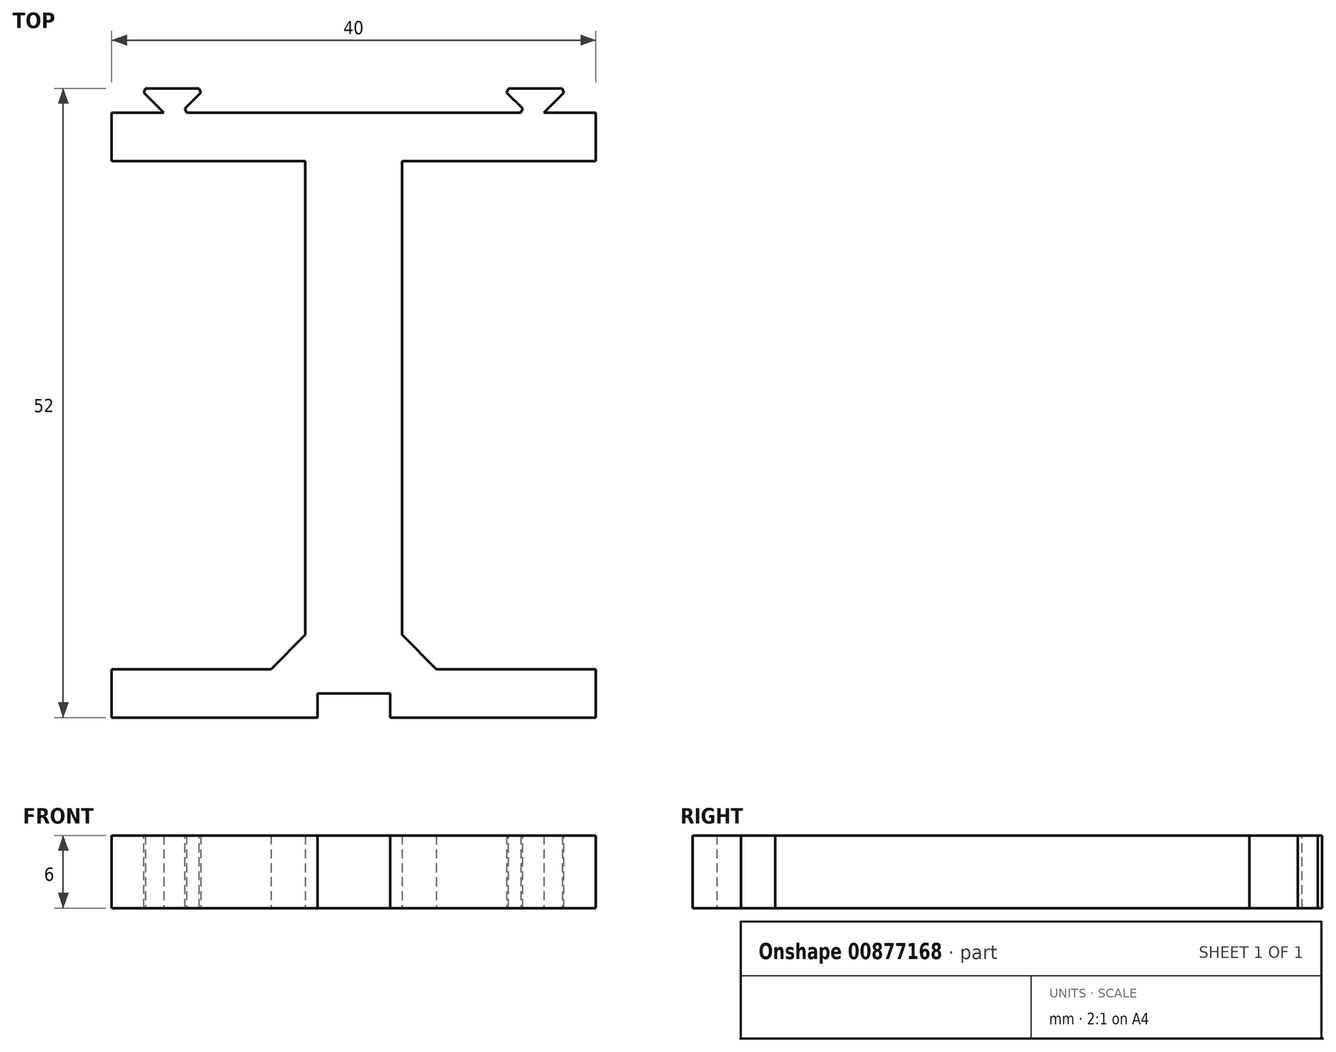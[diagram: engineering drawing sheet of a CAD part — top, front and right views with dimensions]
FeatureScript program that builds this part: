
annotation { "Feature Type Name" : "Feature", "Feature Type Description" : "" }
export const myFeature = defineFeature(function(context is Context, id is Id, definition is map)
    precondition{}
    {
        {
            var Q0;
            Q0=qCreatedBy(makeId("Top.planeOp"),FACE);
            var sketch = newSketch(context, id + "F0", { "sketchPlane" : qUnion([Q0])});
            skLineSegment(sketch, "E0.bottom", {"start": v(0, 0) * mm, "end": v(20, 0) * mm});
            skLineSegment(sketch, "E0.top", {"start": v(0, -50) * mm, "end": v(20, -50) * mm});
            skLineSegment(sketch, "E0.left", {"start": v(0, 0) * mm, "end": v(0, -50) * mm});
            skLineSegment(sketch, "E0.right", {"start": v(20, 0) * mm, "end": v(20, -50) * mm, "construction": true});
            skLineSegment(sketch, "E1.0", {"start": v(4, -46) * mm, "end": v(16, -46) * mm});
            skLineSegment(sketch, "E1.1", {"start": v(4, -4) * mm, "end": v(4, -46) * mm});
            skLineSegment(sketch, "E1.2", {"start": v(4, -4) * mm, "end": v(16, -4) * mm});
            skLineSegment(sketch, "E1.3", {"start": v(16, -4) * mm, "end": v(16, -46) * mm, "construction": true});
            skLineSegment(sketch, "E2", {"start": v(16, -4) * mm, "end": v(20, -4) * mm});
            skLineSegment(sketch, "E3", {"start": v(16, -46) * mm, "end": v(20, -46) * mm});
            skLineSegment(sketch, "E4", {"start": v(20, 0) * mm, "end": v(20, -4) * mm});
            skLineSegment(sketch, "E5", {"start": v(20, -46) * mm, "end": v(20, -50) * mm});
            skLineSegment(sketch, "E6.bottom", {"start": v(0, -50) * mm, "end": v(3, -50) * mm});
            skLineSegment(sketch, "E6.top", {"start": v(0, -48) * mm, "end": v(3, -48) * mm});
            skLineSegment(sketch, "E6.left", {"start": v(0, -50) * mm, "end": v(0, -48) * mm});
            skLineSegment(sketch, "E6.right", {"start": v(3, -50) * mm, "end": v(3, -48) * mm});
            skLineSegment(sketch, "E7", {"start": v(4, -43.17) * mm, "end": v(6.83, -46) * mm});
            skSolve(sketch);
        }
        {
            var Q0;
            {var subQ3=sQuery(id+"F0.wireOp",EDGE,"E7");Q0=makeQuery(id+"F0.imprint","IMPRINT",FACE,{"disambiguationData":[TD([[makeQuery(id+"F0.imprint","IMPRINT",EDGE,{"derivedFrom":subQ3}),-1.0]])]});}
            var Q1;
            Q1=makeQuery(id+"F0.imprint","IMPRINT",FACE,{"disambiguationData":[TD([[makeQuery(id+"F0.imprint","IMPRINT",EDGE,{"derivedFrom":sQuery(id+"F0.wireOp",EDGE,"E0.bottom")}),-1.0]])]});
            extrude(context, id + "F1", {"entities" : qUnion([Q0, Q1]), "depth" : 6 * mm, "offsetDistance" : 25 * mm});
        }
        {
            var Q0;
            Q0=qCreatedBy(makeId("Top.planeOp"),FACE);
            var sketch = newSketch(context, id + "F2", { "sketchPlane" : qUnion([Q0])});
            skLineSegment(sketch, "E8", {"start": v(20, 0) * mm, "end": v(15.7, 0) * mm, "construction": true});
            skLineSegment(sketch, "E9", {"start": v(15.7, 0) * mm, "end": v(17.7, 2) * mm});
            skLineSegment(sketch, "E10", {"start": v(17.7, 2) * mm, "end": v(12.3, 2) * mm});
            skLineSegment(sketch, "E11", {"start": v(12.3, 2) * mm, "end": v(14.3, 0) * mm});
            skLineSegment(sketch, "E12", {"start": v(14.3, 0) * mm, "end": v(15.7, 0) * mm});
            skLineSegment(sketch, "E13", {"start": v(15, 0) * mm, "end": v(15, 2) * mm, "construction": true});
            skSolve(sketch);
        }
        {
            var Q0;
            Q0 = qSketchRegion(id + "F2", true);
            var Q1;
            Q1=makeQuery(id+"F1.opExtrude","CAP_FACE",FACE,{"disambiguationData":[OSD([sQuery(id+"F0.wireOp",EDGE,"E0.bottom"),sQuery(id+"F0.wireOp",EDGE,"E0.top"),sQuery(id+"F0.wireOp",EDGE,"E0.left"),sQuery(id+"F0.wireOp",EDGE,"E1.0"),sQuery(id+"F0.wireOp",EDGE,"E1.1"),sQuery(id+"F0.wireOp",EDGE,"E1.2"),sQuery(id+"F0.wireOp",EDGE,"E2"),sQuery(id+"F0.wireOp",EDGE,"E3"),sQuery(id+"F0.wireOp",EDGE,"E4"),sQuery(id+"F0.wireOp",EDGE,"E5"),sQuery(id+"F0.wireOp",EDGE,"E6.top"),sQuery(id+"F0.wireOp",EDGE,"E6.right"),sQuery(id+"F0.wireOp",EDGE,"E7")])],"isStart":false});
            extrude(context, id + "F3", {"entities" : qUnion([Q0]), "operationType" : NewBodyOperationType.ADD, "endBound" : BoundingType.UP_TO_SURFACE, "depth" : 25 * mm, "endBoundEntityFace" : qUnion([Q1]), "offsetDistance" : 25 * mm});
        }
        {
            var Q0;
            Q0=makeQuery(id+"F3.opExtrude","SWEPT_EDGE",EDGE,{"disambiguationData":[OSD([sQuery(id+"F2.wireOp",EDGE,"E9"),sQuery(id+"F2.wireOp",EDGE,"E10")])]});
            var Q1;
            Q1=makeQuery(id+"F3.opExtrude","SWEPT_EDGE",EDGE,{"disambiguationData":[OSD([sQuery(id+"F2.wireOp",EDGE,"E10"),sQuery(id+"F2.wireOp",EDGE,"E11")])]});
            var Q2;
            Q2=makeQuery(id+"F3.opExtrude","SWEPT_EDGE",EDGE,{"disambiguationData":[OSD([sQuery(id+"F2.wireOp",EDGE,"E9"),sQuery(id+"F2.wireOp",EDGE,"E12")])]});
            var Q3;
            Q3=makeQuery(id+"F3.opExtrude","SWEPT_EDGE",EDGE,{"disambiguationData":[OSD([sQuery(id+"F2.wireOp",EDGE,"E11"),sQuery(id+"F2.wireOp",EDGE,"E12")])]});
            chamfer(context, id + "F4", {"entities" : qUnion([Q0, Q1, Q2, Q3]), "width" : 0.2 * mm, "tangentPropagation" : true});
        }
        {
            var Q0;
            Q0=makeQuery(id+"F1.opExtrude","SWEPT_BODY",BODY,{"disambiguationData":[OSD([sQuery(id+"F0.wireOp",EDGE,"E0.bottom"),sQuery(id+"F0.wireOp",EDGE,"E0.top"),sQuery(id+"F0.wireOp",EDGE,"E0.left"),sQuery(id+"F0.wireOp",EDGE,"E1.0"),sQuery(id+"F0.wireOp",EDGE,"E1.1"),sQuery(id+"F0.wireOp",EDGE,"E1.2"),sQuery(id+"F0.wireOp",EDGE,"E2"),sQuery(id+"F0.wireOp",EDGE,"E3"),sQuery(id+"F0.wireOp",EDGE,"E4"),sQuery(id+"F0.wireOp",EDGE,"E5"),sQuery(id+"F0.wireOp",EDGE,"E6.top"),sQuery(id+"F0.wireOp",EDGE,"E6.right"),sQuery(id+"F0.wireOp",EDGE,"E7")])]});
            var Q1;
            Q1=makeQuery(id+"F1.opExtrude","SWEPT_FACE",FACE,{"disambiguationData":[OSD([sQuery(id+"F0.wireOp",EDGE,"E0.left")])]});
            mirror(context, id + "F5", {"operationType" : NewBodyOperationType.ADD, "entities" : qUnion([Q0]), "mirrorPlane" : qUnion([Q1])});
        }
    });
